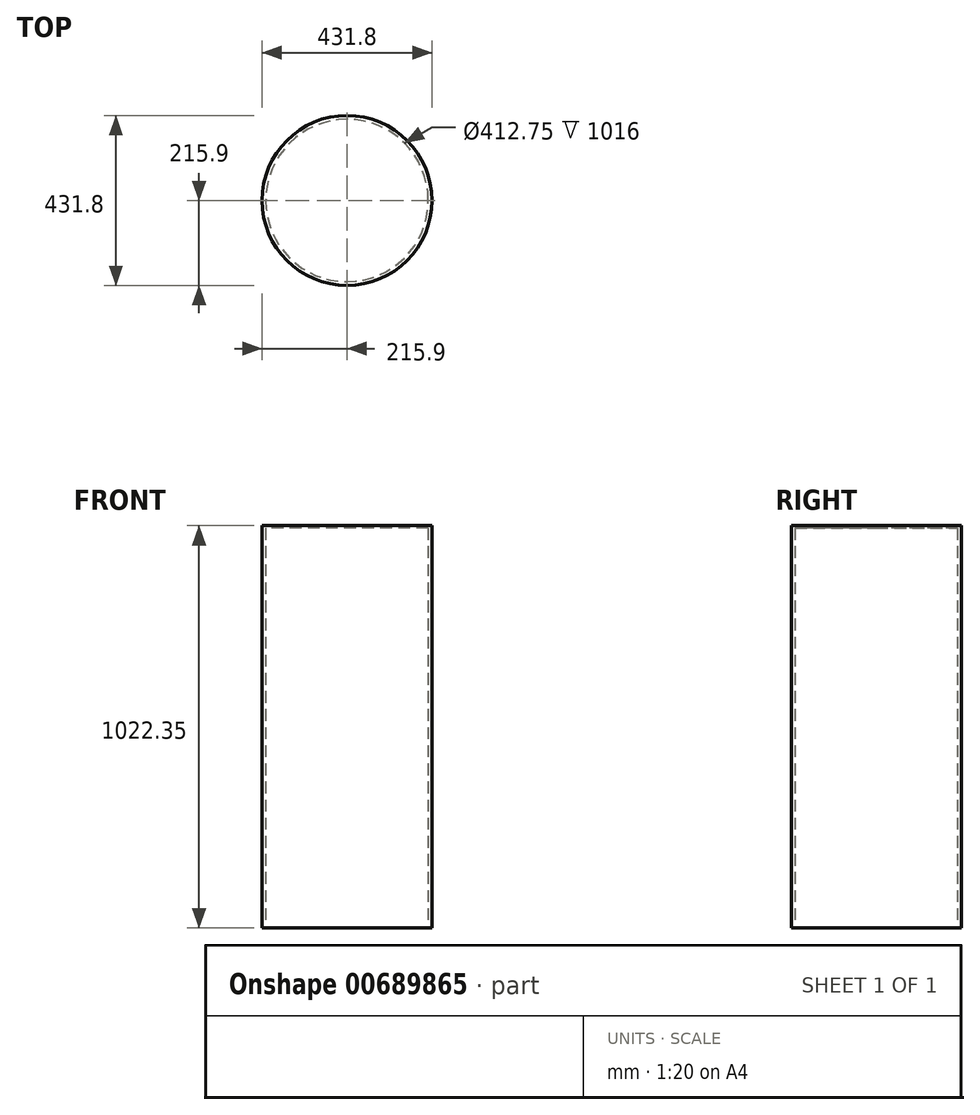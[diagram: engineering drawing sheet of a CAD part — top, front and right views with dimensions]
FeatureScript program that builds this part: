
annotation { "Feature Type Name" : "Feature", "Feature Type Description" : "" }
export const myFeature = defineFeature(function(context is Context, id is Id, definition is map)
    precondition{}
    {
        {
            var Q0;
            Q0=qCreatedBy(makeId("Top.planeOp"),FACE);
            var sketch = newSketch(context, id + "F0", { "sketchPlane" : qUnion([Q0])});
            skCircle(sketch, "E0", {"center": v(0, 0) * mm, "radius": 206.38 * mm});
            skCircle(sketch, "E1.0", {"center": v(0, 0) * mm, "radius": 215.9 * mm});
            skSolve(sketch);
        }
        {
            var Q0;
            Q0 = qSketchRegion(id + "F0", true);
            extrude(context, id + "F1", {"entities" : qUnion([Q0]), "depth" : 457.2 * mm, "offsetDistance" : 25.4 * mm});
        }
        {
            var Q0;
            Q0 = qSketchRegion(id + "F0", true);
            extrude(context, id + "F2", {"entities" : qUnion([Q0]), "operationType" : NewBodyOperationType.ADD, "depth" : 1016 * mm, "offsetDistance" : 25.4 * mm});
        }
        {
            var Q0;
            Q0=makeQuery(id+"F2.opExtrude","CAP_FACE",FACE,{"disambiguationData":[OSD([sQuery(id+"F0.wireOp",EDGE,"E0"),sQuery(id+"F0.wireOp",EDGE,"E1.0")])],"isStart":false});
            var sketch = newSketch(context, id + "F3", { "sketchPlane" : qUnion([Q0])});
            skCircle(sketch, "E2.0", {"center": v(0, 0) * mm, "radius": 215.9 * mm});
            skSolve(sketch);
        }
        {
            var Q0;
            Q0 = qSketchRegion(id + "F3", true);
            extrude(context, id + "F4", {"entities" : qUnion([Q0]), "operationType" : NewBodyOperationType.ADD, "depth" : 6.35 * mm, "offsetDistance" : 25.4 * mm});
        }
    });
